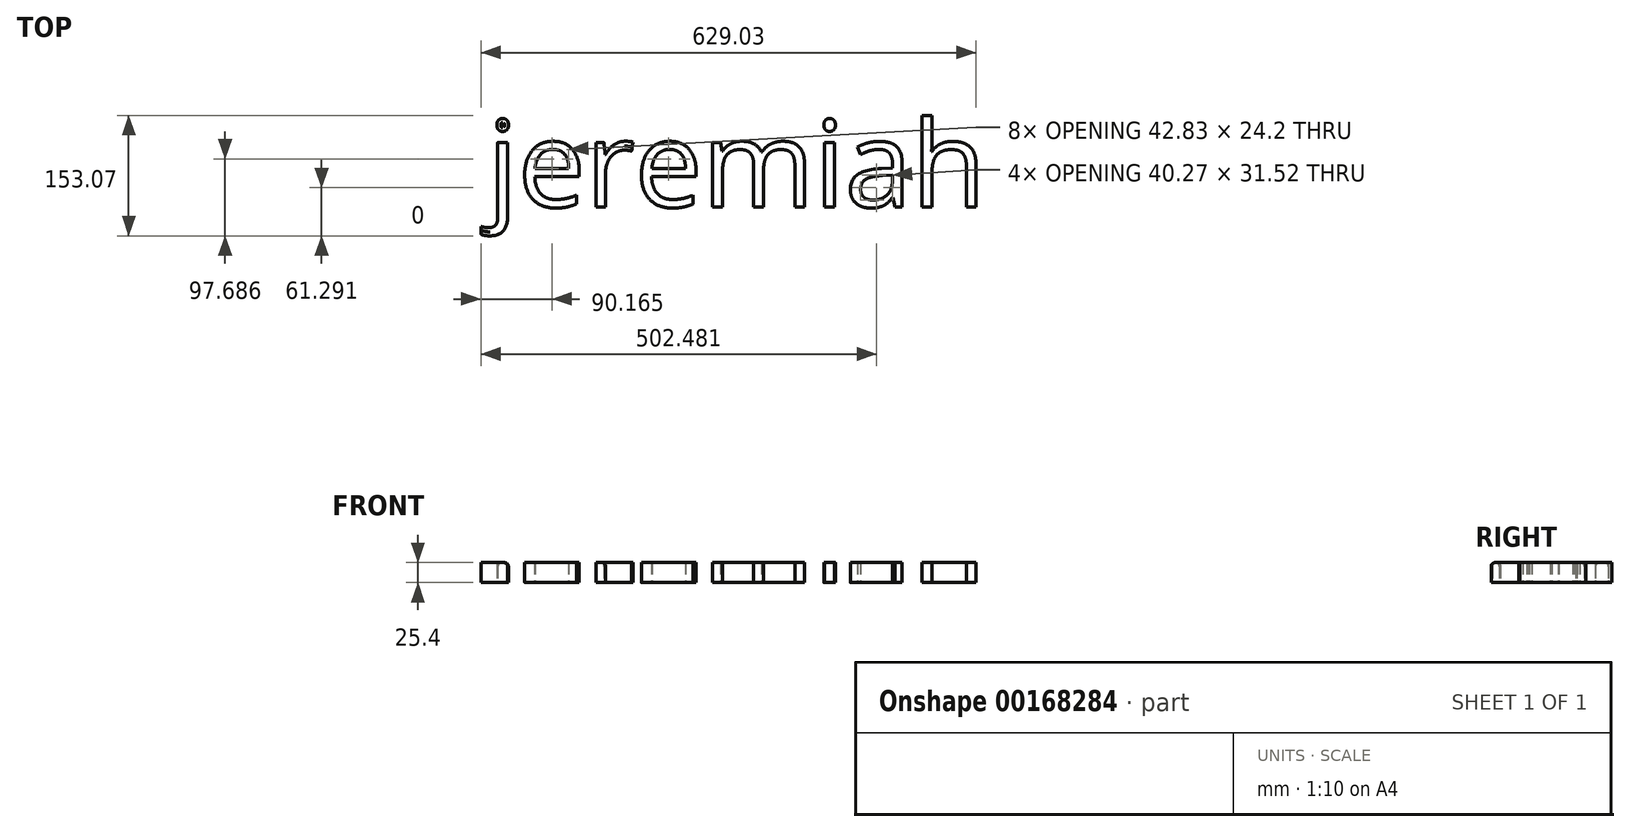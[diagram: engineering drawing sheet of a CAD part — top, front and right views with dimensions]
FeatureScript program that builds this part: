
annotation { "Feature Type Name" : "Feature", "Feature Type Description" : "" }
export const myFeature = defineFeature(function(context is Context, id is Id, definition is map)
    precondition{}
    {
        {
            var Q0;
            Q0=qCreatedBy(makeId("Top.planeOp"),FACE);
            var sketch = newSketch(context, id + "F0", { "sketchPlane" : qUnion([Q0])});
            skText(sketch, "E0", { "text": "jeremiah\n", "fontName": "OpenSans-Regular.ttf"});
            const initialGuessF0  = {"E0": [-0.09388, -0.05715, 1, 0, 0.11019]};
            skSetInitialGuess(sketch, initialGuessF0);
            skSolve(sketch);
        }
        {
            var Q0;
            Q0=makeQuery(id+"F0.imprint","IMPRINT",FACE,{"disambiguationData":[TD([[makeQuery(id+"F0.imprint","IMPRINT",EDGE,{"derivedFrom":sQuery(id+"F0.wireOp",EDGE,"E0.sketch_text.stroke-36")}),-1.0]])]});
            var Q1;
            Q1 = qSketchRegion(id + "F0", true);
            extrude(context, id + "F1", {"entities" : qUnion([Q0, Q1]), "depth" : 25.4 * mm});
        }
        {
            var Q0;
            Q0=makeQuery(id+"F1.opExtrude","CAP_EDGE",EDGE,{"disambiguationData":[OSD([sQuery(id+"F0.wireOp",EDGE,"E0.sketch_text.stroke-5")])],"isStart":false});
            var Q1;
            Q1=makeQuery(id+"F1.opExtrude","CAP_EDGE",EDGE,{"disambiguationData":[OSD([sQuery(id+"F0.wireOp",EDGE,"E0.sketch_text.stroke-7")])],"isStart":false});
            var Q2;
            Q2=makeQuery(id+"F1.opExtrude","CAP_EDGE",EDGE,{"disambiguationData":[OSD([sQuery(id+"F0.wireOp",EDGE,"E0.sketch_text.stroke-26")])],"isStart":false});
            var Q3;
            Q3=makeQuery(id+"F1.opExtrude","CAP_EDGE",EDGE,{"disambiguationData":[OSD([sQuery(id+"F0.wireOp",EDGE,"E0.sketch_text.stroke-17")])],"isStart":false});
            var Q4;
            Q4=makeQuery(id+"F1.opExtrude","CAP_EDGE",EDGE,{"disambiguationData":[OSD([sQuery(id+"F0.wireOp",EDGE,"E0.sketch_text.stroke-33")])],"isStart":false});
            var Q5;
            Q5=makeQuery(id+"F1.opExtrude","CAP_EDGE",EDGE,{"disambiguationData":[OSD([sQuery(id+"F0.wireOp",EDGE,"E0.sketch_text.stroke-24")])],"isStart":false});
            var Q6;
            Q6=makeQuery(id+"F1.opExtrude","CAP_EDGE",EDGE,{"disambiguationData":[OSD([sQuery(id+"F0.wireOp",EDGE,"E0.sketch_text.stroke-41")])],"isStart":false});
            var Q7;
            Q7=makeQuery(id+"F1.opExtrude","CAP_EDGE",EDGE,{"disambiguationData":[OSD([sQuery(id+"F0.wireOp",EDGE,"E0.sketch_text.stroke-40")])],"isStart":false});
            var Q8;
            Q8=makeQuery(id+"F1.opExtrude","CAP_EDGE",EDGE,{"disambiguationData":[OSD([sQuery(id+"F0.wireOp",EDGE,"E0.sketch_text.stroke-44")])],"isStart":false});
            fillet(context, id + "F2", {"entities" : qUnion([Q0, Q1, Q2, Q3, Q4, Q5, Q6, Q7, Q8]), "radius" : 5.08 * mm, "tangentPropagation" : true, "allowEdgeOverflow" : false});
        }
        {
            var Q0;
            Q0=makeQuery(id+"F1.opExtrude","CAP_EDGE",EDGE,{"disambiguationData":[OSD([sQuery(id+"F0.wireOp",EDGE,"E0.sketch_text.stroke-7")])],"isStart":false});
            var Q1;
            Q1=makeQuery(id+"F1.opExtrude","CAP_EDGE",EDGE,{"disambiguationData":[OSD([sQuery(id+"F0.wireOp",EDGE,"E0.sketch_text.stroke-5")])],"isStart":false});
            var Q2;
            Q2=makeQuery(id+"F1.opExtrude","CAP_FACE",FACE,{"disambiguationData":[OSD([sQuery(id+"F0.wireOp",EDGE,"E0.sketch_text.stroke-9"),sQuery(id+"F0.wireOp",EDGE,"E0.sketch_text.stroke-10"),sQuery(id+"F0.wireOp",EDGE,"E0.sketch_text.stroke-11"),sQuery(id+"F0.wireOp",EDGE,"E0.sketch_text.stroke-12"),sQuery(id+"F0.wireOp",EDGE,"E0.sketch_text.stroke-13"),sQuery(id+"F0.wireOp",EDGE,"E0.sketch_text.stroke-14"),sQuery(id+"F0.wireOp",EDGE,"E0.sketch_text.stroke-15"),sQuery(id+"F0.wireOp",EDGE,"E0.sketch_text.stroke-16")])],"isStart":false});
            fillet(context, id + "F3", {"entities" : qUnion([Q0, Q1, Q2]), "radius" : 5.08 * mm, "tangentPropagation" : true, "allowEdgeOverflow" : false});
        }
    });
